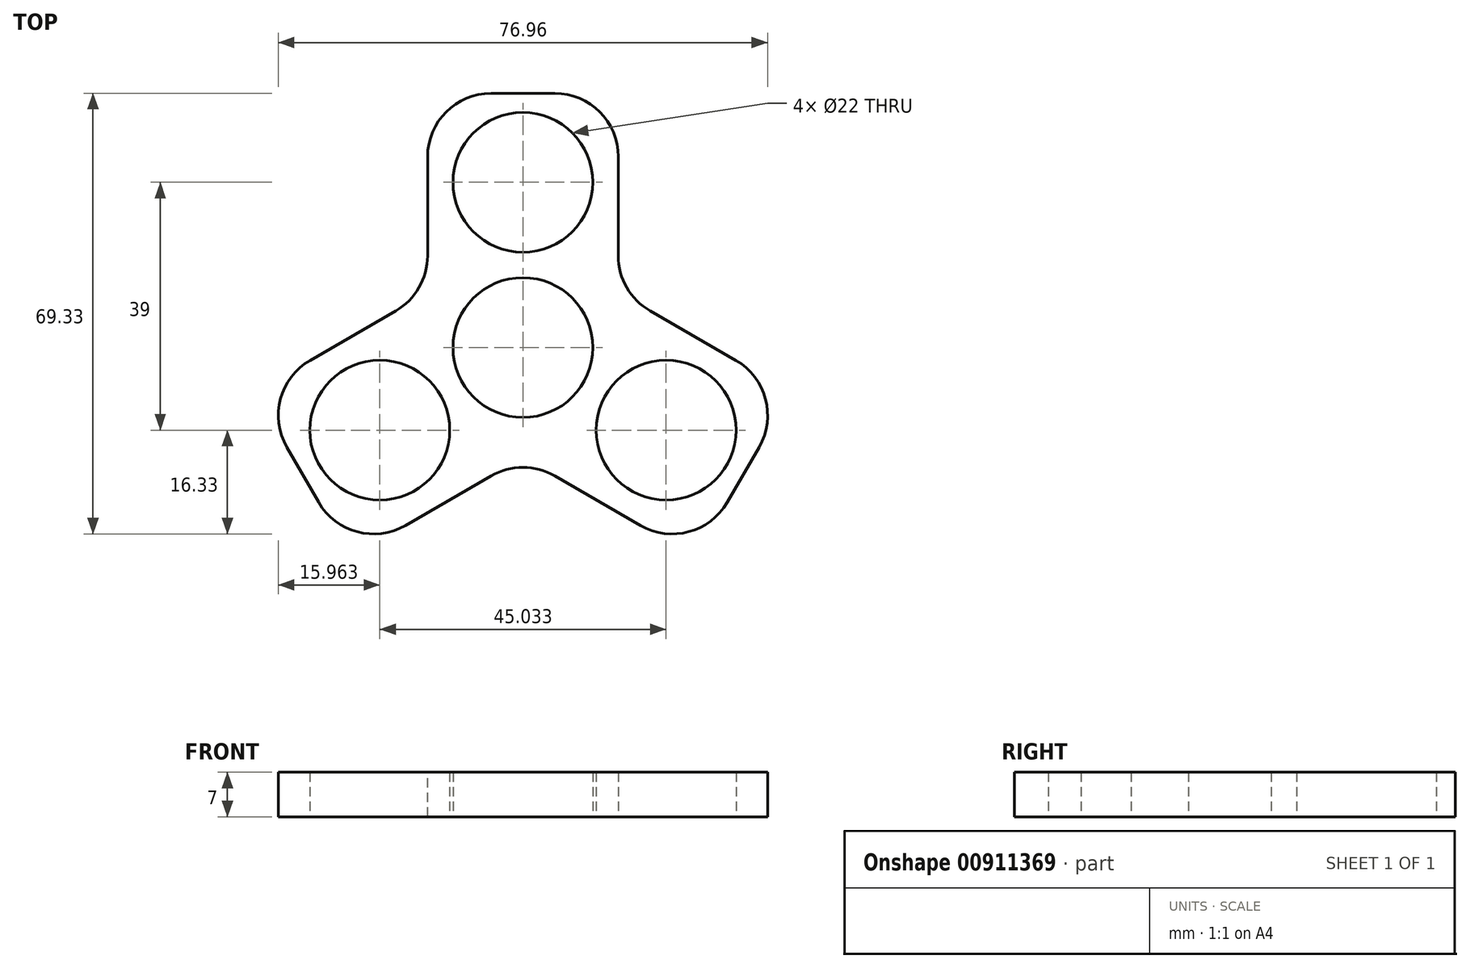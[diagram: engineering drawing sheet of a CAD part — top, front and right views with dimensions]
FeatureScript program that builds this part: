
annotation { "Feature Type Name" : "Feature", "Feature Type Description" : "" }
export const myFeature = defineFeature(function(context is Context, id is Id, definition is map)
    precondition{}
    {
        {
            var Q0;
            Q0=qCreatedBy(makeId("Top.planeOp"),FACE);
            var sketch = newSketch(context, id + "F0", { "sketchPlane" : qUnion([Q0])});
            skCircle(sketch, "E0", {"center": v(0, 0) * mm, "radius": 11 * mm});
            skLineSegment(sketch, "E1.bottom", {"start": v(0, 0) * mm, "end": v(15, 0) * mm});
            skLineSegment(sketch, "E1.top", {"start": v(0, 40) * mm, "end": v(15, 40) * mm});
            skLineSegment(sketch, "E1.left", {"start": v(0, 0) * mm, "end": v(0, 40) * mm});
            skLineSegment(sketch, "E1.right", {"start": v(15, 0) * mm, "end": v(15, 40) * mm});
            skLineSegment(sketch, "E2.bottom", {"start": v(0, 0) * mm, "end": v(-15, 0) * mm});
            skLineSegment(sketch, "E2.top", {"start": v(0, 40) * mm, "end": v(-15, 40) * mm});
            skLineSegment(sketch, "E2.right", {"start": v(-15, 0) * mm, "end": v(-15, 40) * mm});
            skLineSegment(sketch, "E3", {"start": v(0, 40) * mm, "end": v(0, 26) * mm});
            skCircle(sketch, "E4", {"center": v(0, 26) * mm, "radius": 11 * mm});
            skSolve(sketch);
        }
        {
            var Q0;
            {var subQ0=sQuery(id+"F0.wireOp",EDGE,"E2.top");Q0=makeQuery(id+"F0.imprint","IMPRINT",FACE,{"disambiguationData":[TD([[makeQuery(id+"F0.imprint","IMPRINT",EDGE,{"derivedFrom":subQ0}),1.0]])]});}
            var Q1;
            {var subQ9=sQuery(id+"F0.wireOp",EDGE,"E1.top");Q1=makeQuery(id+"F0.imprint","IMPRINT",FACE,{"disambiguationData":[TD([[makeQuery(id+"F0.imprint","IMPRINT",EDGE,{"derivedFrom":subQ9}),-1.0]])]});}
            extrude(context, id + "F1", {"entities" : qUnion([Q0, Q1]), "depth" : 7 * mm, "offsetDistance" : 25 * mm});
        }
        {
            var Q0;
            Q0=qCreatedBy(makeId("Front.planeOp"),FACE);
            var sketch = newSketch(context, id + "F2", { "sketchPlane" : qUnion([Q0])});
            skLineSegment(sketch, "E5", {"start": v(0, 0) * mm, "end": v(0, 52.14) * mm});
            skSolve(sketch);
        }
        {
            var Q0;
            Q0=makeQuery(id+"F1.opExtrude","SWEPT_BODY",BODY,{"disambiguationData":[OSD([sQuery(id+"F0.wireOp",EDGE,"E0"),sQuery(id+"F0.wireOp",EDGE,"E1.bottom"),sQuery(id+"F0.wireOp",EDGE,"E1.top"),sQuery(id+"F0.wireOp",EDGE,"E1.right"),sQuery(id+"F0.wireOp",EDGE,"E2.bottom"),sQuery(id+"F0.wireOp",EDGE,"E2.top"),sQuery(id+"F0.wireOp",EDGE,"E2.right"),sQuery(id+"F0.wireOp",EDGE,"E4")])]});
            var Q1;
            Q1=sQuery(id+"F2.wireOp",EDGE,"E5");
            transform(context, id + "F3", {"entities" : qUnion([Q0]), "transformType" : TransformType.ROTATION, "transformAxis" : qUnion([Q1]), "angle" : 120 * degree, "makeCopy" : true});
        }
        {
            var Q0;
            Q0=makeQuery(id+"F1.opExtrude","SWEPT_BODY",BODY,{"disambiguationData":[OSD([sQuery(id+"F0.wireOp",EDGE,"E0"),sQuery(id+"F0.wireOp",EDGE,"E1.bottom"),sQuery(id+"F0.wireOp",EDGE,"E1.top"),sQuery(id+"F0.wireOp",EDGE,"E1.right"),sQuery(id+"F0.wireOp",EDGE,"E2.bottom"),sQuery(id+"F0.wireOp",EDGE,"E2.top"),sQuery(id+"F0.wireOp",EDGE,"E2.right"),sQuery(id+"F0.wireOp",EDGE,"E4")])]});
            var Q1;
            Q1=sQuery(id+"F2.wireOp",EDGE,"E5");
            transform(context, id + "F4", {"entities" : qUnion([Q0]), "transformType" : TransformType.ROTATION, "transformAxis" : qUnion([Q1]), "angle" : 240 * degree, "makeCopy" : true});
        }
        {
            var Q0;
            Q0=makeQuery(id+"F1.opExtrude","SWEPT_BODY",BODY,{"disambiguationData":[OSD([sQuery(id+"F0.wireOp",EDGE,"E0"),sQuery(id+"F0.wireOp",EDGE,"E1.bottom"),sQuery(id+"F0.wireOp",EDGE,"E1.top"),sQuery(id+"F0.wireOp",EDGE,"E1.right"),sQuery(id+"F0.wireOp",EDGE,"E2.bottom"),sQuery(id+"F0.wireOp",EDGE,"E2.top"),sQuery(id+"F0.wireOp",EDGE,"E2.right"),sQuery(id+"F0.wireOp",EDGE,"E4")])]});
            var Q1;
            Q1=makeQuery(id+"F4.opPattern","COPY",BODY,{"derivedFrom":makeQuery(id+"F1.opExtrude","SWEPT_BODY",BODY,{"disambiguationData":[OSD([sQuery(id+"F0.wireOp",EDGE,"E0"),sQuery(id+"F0.wireOp",EDGE,"E1.bottom"),sQuery(id+"F0.wireOp",EDGE,"E1.top"),sQuery(id+"F0.wireOp",EDGE,"E1.right"),sQuery(id+"F0.wireOp",EDGE,"E2.bottom"),sQuery(id+"F0.wireOp",EDGE,"E2.top"),sQuery(id+"F0.wireOp",EDGE,"E2.right"),sQuery(id+"F0.wireOp",EDGE,"E4")])]}),"instanceName":"1"});
            var Q2;
            Q2=makeQuery(id+"F3.opPattern","COPY",BODY,{"derivedFrom":makeQuery(id+"F1.opExtrude","SWEPT_BODY",BODY,{"disambiguationData":[OSD([sQuery(id+"F0.wireOp",EDGE,"E0"),sQuery(id+"F0.wireOp",EDGE,"E1.bottom"),sQuery(id+"F0.wireOp",EDGE,"E1.top"),sQuery(id+"F0.wireOp",EDGE,"E1.right"),sQuery(id+"F0.wireOp",EDGE,"E2.bottom"),sQuery(id+"F0.wireOp",EDGE,"E2.top"),sQuery(id+"F0.wireOp",EDGE,"E2.right"),sQuery(id+"F0.wireOp",EDGE,"E4")])]}),"instanceName":"1"});
            booleanBodies(context, id + "F5", {"operationType" : BooleanOperationType.UNION, "tools" : qUnion([Q0, Q1, Q2])});
        }
        {
            var Q0;
            Q0=makeQuery(id+"F1.opExtrude","SWEPT_EDGE",EDGE,{"disambiguationData":[OSD([sQuery(id+"F0.wireOp",EDGE,"E1.top"),sQuery(id+"F0.wireOp",EDGE,"E1.right")])]});
            var Q1;
            Q1=makeQuery(id+"F4.opPattern","COPY",EDGE,{"derivedFrom":makeQuery(id+"F1.opExtrude","SWEPT_EDGE",EDGE,{"disambiguationData":[OSD([sQuery(id+"F0.wireOp",EDGE,"E2.top"),sQuery(id+"F0.wireOp",EDGE,"E2.right")])]}),"instanceName":"1"});
            var Q2;
            Q2=makeQuery(id+"F4.opPattern","COPY",EDGE,{"derivedFrom":makeQuery(id+"F1.opExtrude","SWEPT_EDGE",EDGE,{"disambiguationData":[OSD([sQuery(id+"F0.wireOp",EDGE,"E1.top"),sQuery(id+"F0.wireOp",EDGE,"E1.right")])]}),"instanceName":"1"});
            var Q3;
            Q3=makeQuery(id+"F3.opPattern","COPY",EDGE,{"derivedFrom":makeQuery(id+"F1.opExtrude","SWEPT_EDGE",EDGE,{"disambiguationData":[OSD([sQuery(id+"F0.wireOp",EDGE,"E2.top"),sQuery(id+"F0.wireOp",EDGE,"E2.right")])]}),"instanceName":"1"});
            var Q4;
            Q4=makeQuery(id+"F3.opPattern","COPY",EDGE,{"derivedFrom":makeQuery(id+"F1.opExtrude","SWEPT_EDGE",EDGE,{"disambiguationData":[OSD([sQuery(id+"F0.wireOp",EDGE,"E1.top"),sQuery(id+"F0.wireOp",EDGE,"E1.right")])]}),"instanceName":"1"});
            var Q5;
            Q5=makeQuery(id+"F1.opExtrude","SWEPT_EDGE",EDGE,{"disambiguationData":[OSD([sQuery(id+"F0.wireOp",EDGE,"E2.top"),sQuery(id+"F0.wireOp",EDGE,"E2.right")])]});
            var Q6;
            Q6=makeQuery(id+"F5.opBoolean","INTERSECT",EDGE,{"derivedFrom":[makeQuery(id+"F1.opExtrude","SWEPT_FACE",FACE,{"disambiguationData":[OSD([sQuery(id+"F0.wireOp",EDGE,"E2.right")])]}),makeQuery(id+"F3.opPattern","COPY",FACE,{"derivedFrom":makeQuery(id+"F1.opExtrude","SWEPT_FACE",FACE,{"disambiguationData":[OSD([sQuery(id+"F0.wireOp",EDGE,"E1.right")])]}),"instanceName":"1"})]});
            var Q7;
            Q7=makeQuery(id+"F5.opBoolean","INTERSECT",EDGE,{"derivedFrom":[makeQuery(id+"F3.opPattern","COPY",FACE,{"derivedFrom":makeQuery(id+"F1.opExtrude","SWEPT_FACE",FACE,{"disambiguationData":[OSD([sQuery(id+"F0.wireOp",EDGE,"E2.right")])]}),"instanceName":"1"}),makeQuery(id+"F4.opPattern","COPY",FACE,{"derivedFrom":makeQuery(id+"F1.opExtrude","SWEPT_FACE",FACE,{"disambiguationData":[OSD([sQuery(id+"F0.wireOp",EDGE,"E1.right")])]}),"instanceName":"1"})]});
            var Q8;
            Q8=makeQuery(id+"F5.opBoolean","INTERSECT",EDGE,{"derivedFrom":[makeQuery(id+"F1.opExtrude","SWEPT_FACE",FACE,{"disambiguationData":[OSD([sQuery(id+"F0.wireOp",EDGE,"E1.right")])]}),makeQuery(id+"F4.opPattern","COPY",FACE,{"derivedFrom":makeQuery(id+"F1.opExtrude","SWEPT_FACE",FACE,{"disambiguationData":[OSD([sQuery(id+"F0.wireOp",EDGE,"E2.right")])]}),"instanceName":"1"})]});
            fillet(context, id + "F6", {"entities" : qUnion([Q0, Q1, Q2, Q3, Q4, Q5, Q6, Q7, Q8]), "radius" : 10 * mm, "tangentPropagation" : true, "allowEdgeOverflow" : false});
        }
    });
